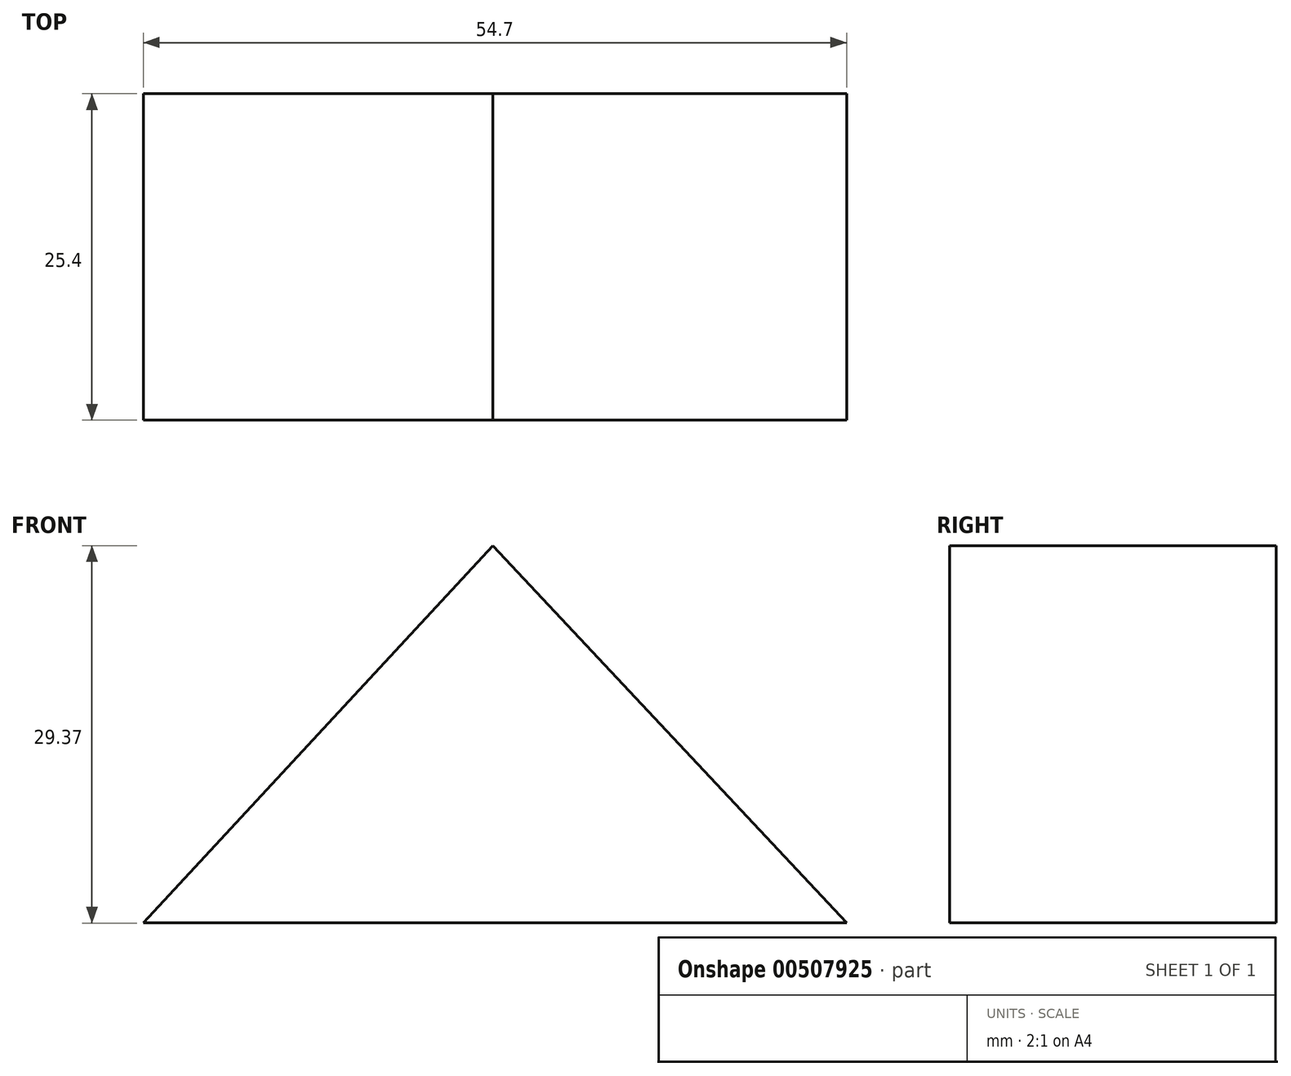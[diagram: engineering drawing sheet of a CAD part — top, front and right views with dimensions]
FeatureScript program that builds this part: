
annotation { "Feature Type Name" : "Feature", "Feature Type Description" : "" }
export const myFeature = defineFeature(function(context is Context, id is Id, definition is map)
    precondition{}
    {
        {
            var Q0;
            Q0=qCreatedBy(makeId("Front.planeOp"),FACE);
            var sketch = newSketch(context, id + "F0", { "sketchPlane" : qUnion([Q0])});
            skLineSegment(sketch, "E0", {"start": v(27.53, 9.3) * mm, "end": v(-27.17, 9.3) * mm});
            skLineSegment(sketch, "E1", {"start": v(-27.17, 9.3) * mm, "end": v(0, 38.66) * mm});
            skLineSegment(sketch, "E2", {"start": v(27.53, 9.3) * mm, "end": v(0, 38.66) * mm});
            skLineSegment(sketch, "E3", {"start": v(0, 38.66) * mm, "end": v(0, 9.3) * mm});
            skSolve(sketch);
        }
        {
            var Q0;
            Q0 = qSketchRegion(id + "F0", true);
            extrude(context, id + "F1", {"entities" : qUnion([Q0]), "depth" : 25.4 * mm});
        }
    });
